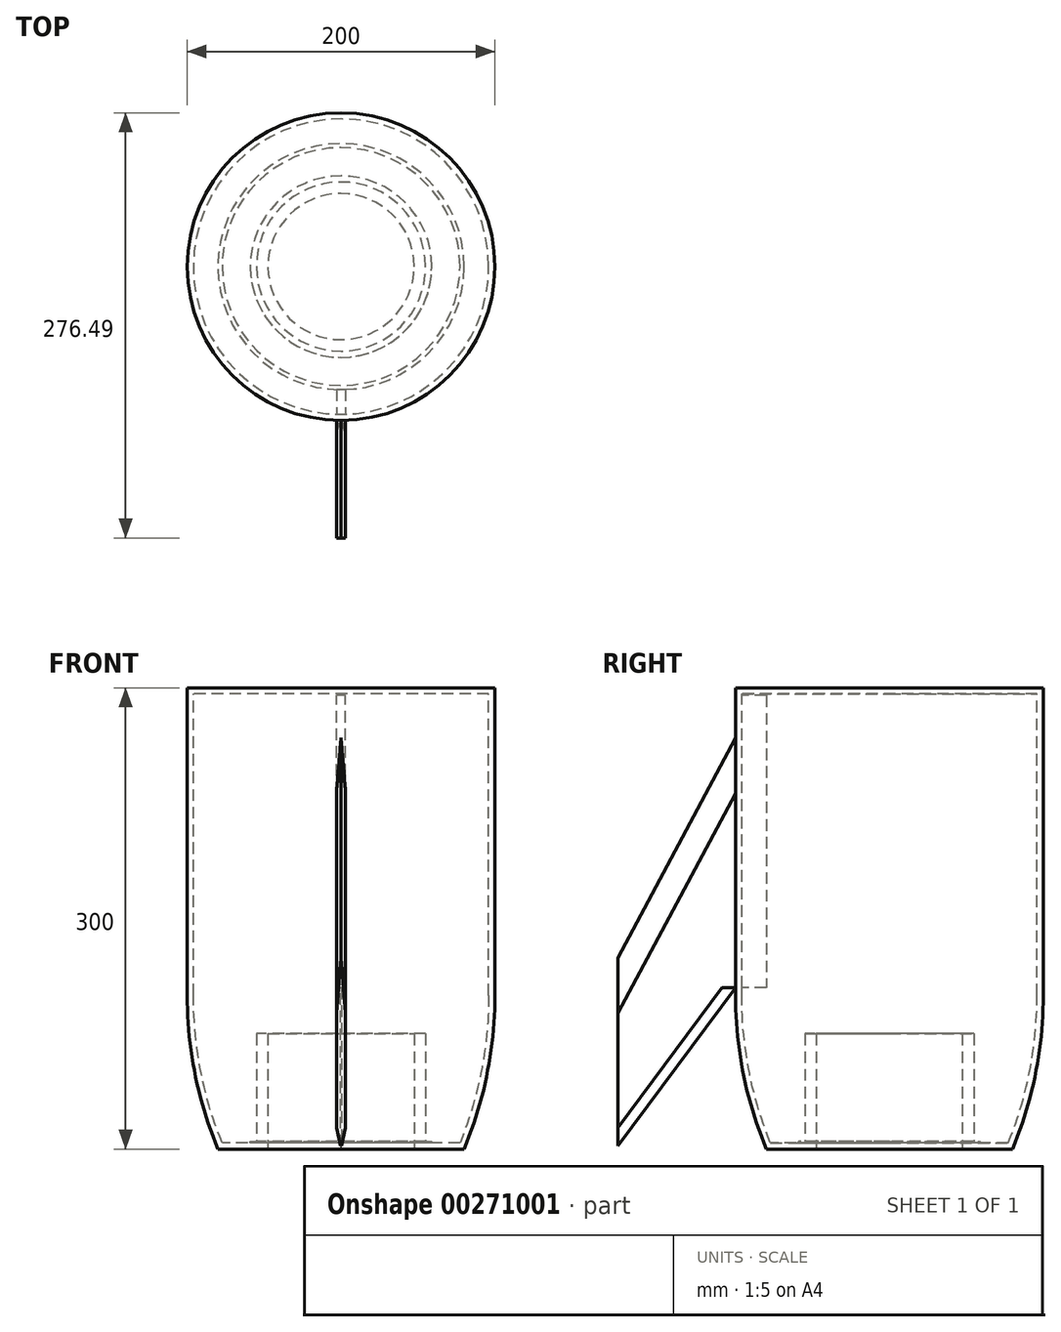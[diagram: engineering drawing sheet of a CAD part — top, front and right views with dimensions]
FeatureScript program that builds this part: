
annotation { "Feature Type Name" : "Feature", "Feature Type Description" : "" }
export const myFeature = defineFeature(function(context is Context, id is Id, definition is map)
    precondition{}
    {
        {
            var Q0;
            Q0=qCreatedBy(makeId("Front.planeOp"),FACE);
            var sketch = newSketch(context, id + "F0", { "sketchPlane" : qUnion([Q0])});
            skLineSegment(sketch, "E0", {"start": v(0, 300) * mm, "end": v(-100, 300) * mm});
            skLineSegment(sketch, "E1", {"start": v(-100, 300) * mm, "end": v(-100, 100) * mm});
            skArc(sketch, "E2", {"start": v(-100, 100) * mm, "mid": v(-94.95, 49) * mm, "end": v(-80, 0) * mm});
            skLineSegment(sketch, "E3", {"start": v(-55, 5) * mm, "end": v(0, 5) * mm});
            skLineSegment(sketch, "E4", {"start": v(-55, 5) * mm, "end": v(-55, 0) * mm});
            skLineSegment(sketch, "E5", {"start": v(0, 300) * mm, "end": v(0, 5) * mm});
            skLineSegment(sketch, "E6", {"start": v(-55, 0) * mm, "end": v(-80, 0) * mm});
            skSolve(sketch);
        }
        {
            var Q0;
            Q0=makeQuery(id+"F0.imprint","IMPRINT",FACE,{"disambiguationData":[TD([[makeQuery(id+"F0.imprint","IMPRINT",EDGE,{"derivedFrom":sQuery(id+"F0.wireOp",EDGE,"E0")}),1.0]])]});
            var Q1;
            Q1=sQuery(id+"F0.wireOp",EDGE,"E5");
            revolve(context, id + "F1", {"entities" : qUnion([Q0]), "axis" : qUnion([Q1]), "revolveType" : RevolveType.FULL});
        }
        {
            var Q0;
            Q0=makeQuery(id+"F1.opRevolve","SWEPT_FACE",FACE,{"disambiguationData":[OSD([sQuery(id+"F0.wireOp",EDGE,"E3")])]});
            shell(context, id + "F2", {"entities" : qUnion([Q0]), "thickness" : 4 * mm});
        }
        {
            var Q0;
            Q0=qCreatedBy(makeId("Right.planeOp"),FACE);
            var sketch = newSketch(context, id + "F3", { "sketchPlane" : qUnion([Q0])});
            skLineSegment(sketch, "E7.bottom", {"start": v(-80, 295) * mm, "end": v(-100, 295) * mm});
            skLineSegment(sketch, "E8", {"start": v(-100, 295) * mm, "end": v(-176.49, 151.95) * mm});
            skLineSegment(sketch, "E9", {"start": v(-176.49, 151.95) * mm, "end": v(-176.49, 1.95) * mm});
            skLineSegment(sketch, "E10", {"start": v(-176.49, 1.95) * mm, "end": v(-100, 105) * mm});
            skLineSegment(sketch, "E11", {"start": v(-80, 295) * mm, "end": v(-80, 105) * mm});
            skLineSegment(sketch, "E12", {"start": v(-80, 105) * mm, "end": v(-100, 105) * mm});
            skSolve(sketch);
        }
        {
            var Q0;
            {var subQ1=sQuery(id+"F3.wireOp",EDGE,"1s16eoF1-X7h5-zxAd-6RXK-nLReMDBOlljz.left");Q0=makeQuery(id+"F3.imprint","IMPRINT",FACE,{"disambiguationData":[TD([[makeQuery(id+"F3.imprint","IMPRINT",EDGE,{"derivedFrom":subQ1}),-1.0]])]});}
            var Q1;
            Q1=makeQuery(id+"F3.imprint","IMPRINT",FACE,{"disambiguationData":[TD([[makeQuery(id+"F3.imprint","IMPRINT",EDGE,{"derivedFrom":sQuery(id+"F3.wireOp",EDGE,"E7.bottom")}),1.0]])]});
            extrude(context, id + "F4", {"entities" : qUnion([Q0, Q1]), "operationType" : NewBodyOperationType.ADD, "depth" : 3 * mm, "hasSecondDirection" : true, "secondDirectionOppositeDirection" : true, "secondDirectionDepth" : 3 * mm});
        }
        {
            var Q0;
            Q0=makeQuery(id+"F4.opExtrude","CAP_EDGE",EDGE,{"disambiguationData":[OSD([sQuery(id+"F3.wireOp",EDGE,"E8")])],"isStart":false});
            var Q1;
            Q1=makeQuery(id+"F4.opExtrude","CAP_EDGE",EDGE,{"disambiguationData":[OSD([sQuery(id+"F3.wireOp",EDGE,"E8")])],"isStart":true});
            chamfer(context, id + "F5", {"entities" : qUnion([Q0, Q1]), "chamferType" : ChamferType.OFFSET_ANGLE, "width" : 30 * mm, "oppositeDirection" : false, "angle" : 10 * degree, "tangentPropagation" : true});
        }
        {
            var Q0;
            Q0=makeQuery(id+"F4.opExtrude","CAP_EDGE",EDGE,{"disambiguationData":[OSD([sQuery(id+"F3.wireOp",EDGE,"E10")])],"isStart":false});
            var Q1;
            Q1=makeQuery(id+"F4.opExtrude","CAP_EDGE",EDGE,{"disambiguationData":[OSD([sQuery(id+"F3.wireOp",EDGE,"E10")])],"isStart":true});
            chamfer(context, id + "F6", {"entities" : qUnion([Q0, Q1]), "chamferType" : ChamferType.OFFSET_ANGLE, "width" : 7 * mm, "oppositeDirection" : false, "angle" : 20 * degree, "tangentPropagation" : true});
        }
        {
            var Q0;
            Q0=makeQuery(id+"F1.opRevolve","SWEPT_FACE",FACE,{"disambiguationData":[OSD([sQuery(id+"F0.wireOp",EDGE,"E6")])]});
            var sketch = newSketch(context, id + "F7", { "sketchPlane" : qUnion([Q0])});
            skCircle(sketch, "E13", {"center": v(0, 0) * mm, "radius": 57.5 * mm});
            skCircle(sketch, "E14", {"center": v(0, 0) * mm, "radius": 47.5 * mm});
            skSolve(sketch);
        }
        {
            var Q0;
            Q0=makeQuery(id+"F7.imprint","IMPRINT",FACE,{"disambiguationData":[TD([[makeQuery(id+"F7.imprint","IMPRINT",EDGE,{"derivedFrom":sQuery(id+"F7.wireOp",EDGE,"E14")}),-1.0]])]});
            extrude(context, id + "F8", {"entities" : qUnion([Q0]), "operationType" : NewBodyOperationType.ADD, "oppositeDirection" : true, "depth" : 75 * mm});
        }
    });
